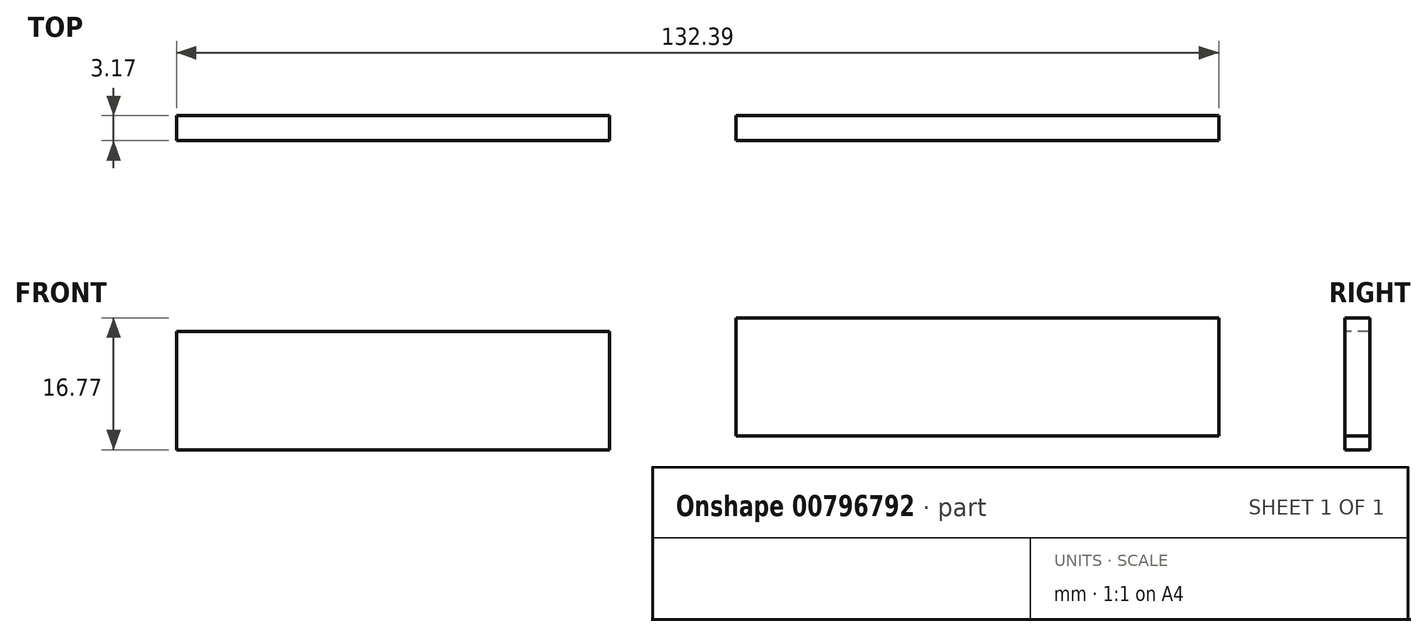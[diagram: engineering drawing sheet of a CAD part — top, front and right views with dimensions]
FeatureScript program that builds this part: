
annotation { "Feature Type Name" : "Feature", "Feature Type Description" : "" }
export const myFeature = defineFeature(function(context is Context, id is Id, definition is map)
    precondition{}
    {
        {
            var Q0;
            Q0=qCreatedBy(makeId("Front.planeOp"),FACE);
            var sketch = newSketch(context, id + "F0", { "sketchPlane" : qUnion([Q0])});
            skLineSegment(sketch, "E0.bottom", {"start": v(-55, 0) * mm, "end": v(0, 0) * mm});
            skLineSegment(sketch, "E0.top", {"start": v(-55, -15) * mm, "end": v(0, -15) * mm});
            skLineSegment(sketch, "E0.left", {"start": v(-55, 0) * mm, "end": v(-55, -15) * mm});
            skLineSegment(sketch, "E0.right", {"start": v(0, 0) * mm, "end": v(0, -15) * mm});
            skLineSegment(sketch, "E1.bottom", {"start": v(16.04, 1.77) * mm, "end": v(77.4, 1.77) * mm});
            skLineSegment(sketch, "E1.top", {"start": v(16.04, -13.23) * mm, "end": v(77.4, -13.23) * mm});
            skLineSegment(sketch, "E1.left", {"start": v(16.04, 1.77) * mm, "end": v(16.04, -13.23) * mm});
            skLineSegment(sketch, "E1.right", {"start": v(77.4, 1.77) * mm, "end": v(77.4, -13.23) * mm});
            skSolve(sketch);
        }
        {
            var Q0;
            Q0=makeQuery(id+"F0.imprint","IMPRINT",FACE,{"disambiguationData":[TD([[makeQuery(id+"F0.imprint","IMPRINT",EDGE,{"derivedFrom":sQuery(id+"F0.wireOp",EDGE,"E0.bottom")}),-1.0]])]});
            var Q1;
            Q1=makeQuery(id+"F0.imprint","IMPRINT",FACE,{"disambiguationData":[TD([[makeQuery(id+"F0.imprint","IMPRINT",EDGE,{"derivedFrom":sQuery(id+"F0.wireOp",EDGE,"E1.bottom")}),-1.0]])]});
            extrude(context, id + "F1", {"entities" : qUnion([Q0, Q1]), "oppositeDirection" : true, "depth" : 3.17 * mm, "offsetDistance" : 25.4 * mm});
        }
    });
